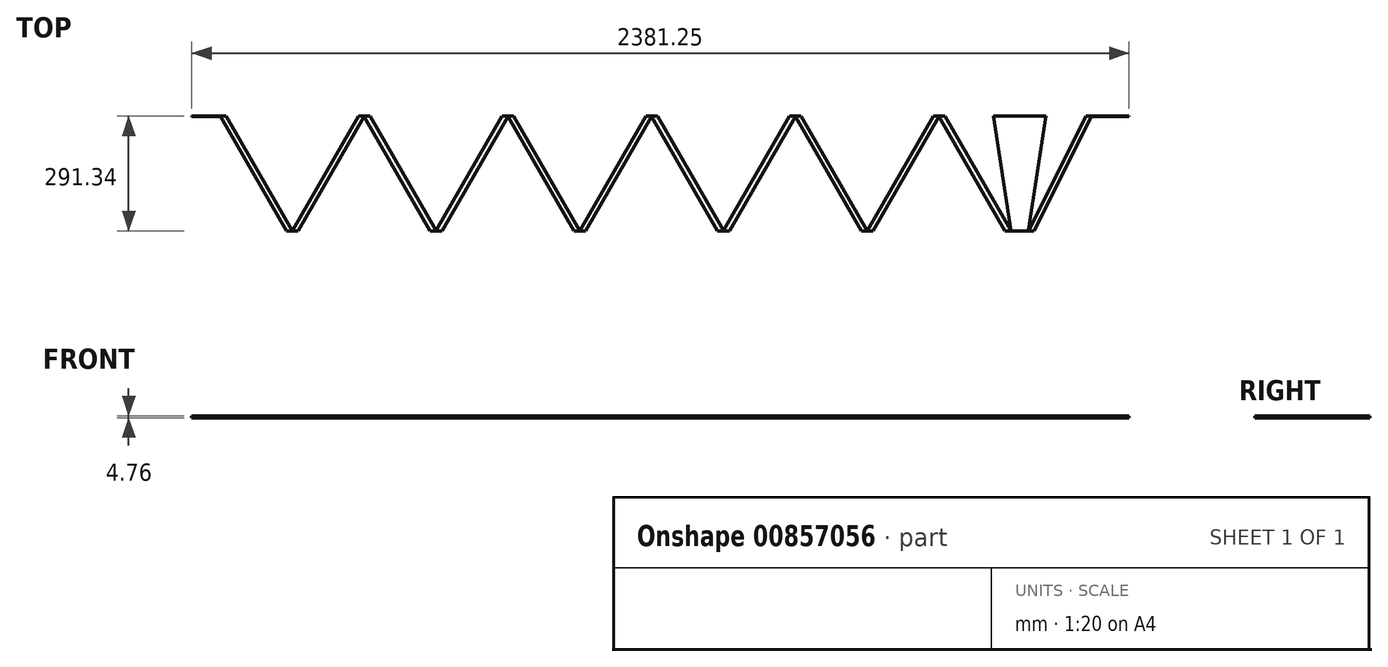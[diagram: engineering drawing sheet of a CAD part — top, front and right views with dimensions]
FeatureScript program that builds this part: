
annotation { "Feature Type Name" : "Feature", "Feature Type Description" : "" }
export const myFeature = defineFeature(function(context is Context, id is Id, definition is map)
    precondition{}
    {
        {
            var Q0;
            Q0=qCreatedBy(makeId("Top.planeOp"),FACE);
            var sketch = newSketch(context, id + "F0", { "sketchPlane" : qUnion([Q0])});
            skLineSegment(sketch, "E0.bottom", {"start": v(-1203.33, 145.67) * mm, "end": v(1203.33, 145.67) * mm});
            skLineSegment(sketch, "E0.top", {"start": v(-1203.33, -145.67) * mm, "end": v(1203.33, -145.67) * mm});
            skLineSegment(sketch, "E0.left", {"start": v(-1203.33, 145.67) * mm, "end": v(-1203.33, -145.67) * mm});
            skLineSegment(sketch, "E0.right", {"start": v(1203.33, 145.67) * mm, "end": v(1203.33, -145.67) * mm});
            skPoint(sketch, "E0.middle", {"position": v(0, 0) * mm});
            skPoint(sketch, "E1", {"position": v(0, 145.67) * mm});
            skPoint(sketch, "E2", {"position": v(0, -145.67) * mm});
            skPoint(sketch, "E3", {"position": v(182.56, -145.67) * mm});
            skPoint(sketch, "E4.MirrorP", {"position": v(-182.56, -145.67) * mm});
            skPoint(sketch, "E5", {"position": v(365.12, 145.67) * mm});
            skPoint(sketch, "E6", {"position": v(547.69, -145.67) * mm});
            skPoint(sketch, "E7", {"position": v(730.25, 145.67) * mm});
            skPoint(sketch, "E8", {"position": v(912.81, -145.67) * mm});
            skPoint(sketch, "E9", {"position": v(935.04, -145.67) * mm});
            skPoint(sketch, "E10", {"position": v(957.26, -145.67) * mm});
            skPoint(sketch, "E11", {"position": v(1117.6, 145.67) * mm});
            skLineSegment(sketch, "E12", {"start": v(0.22, 145.29) * mm, "end": v(167.9, -145.67) * mm});
            skLineSegment(sketch, "E13", {"start": v(182.34, -145.29) * mm, "end": v(14.66, 145.67) * mm});
            skLineSegment(sketch, "E14", {"start": v(182.78, -145.29) * mm, "end": v(350.47, 145.67) * mm});
            skLineSegment(sketch, "E15", {"start": v(364.9, 145.29) * mm, "end": v(197.22, -145.67) * mm});
            skLineSegment(sketch, "E16", {"start": v(365.35, 145.29) * mm, "end": v(533.03, -145.67) * mm});
            skLineSegment(sketch, "E17", {"start": v(547.47, -145.29) * mm, "end": v(379.78, 145.67) * mm});
            skLineSegment(sketch, "E18", {"start": v(547.9, -145.29) * mm, "end": v(715.6, 145.67) * mm});
            skLineSegment(sketch, "E19", {"start": v(730.03, 145.29) * mm, "end": v(562.35, -145.67) * mm});
            skLineSegment(sketch, "E20", {"start": v(730.47, 145.29) * mm, "end": v(898.15, -145.67) * mm});
            skLineSegment(sketch, "E21", {"start": v(912.14, -144.5) * mm, "end": v(744.9, 145.67) * mm});
            skLineSegment(sketch, "E22", {"start": v(957.98, -144.23) * mm, "end": v(1103.4, 145.67) * mm});
            skLineSegment(sketch, "E23", {"start": v(1117.6, 145.67) * mm, "end": v(971.47, -145.67) * mm});
            skLineSegment(sketch, "E24", {"start": v(-0.22, 145.29) * mm, "end": v(-167.9, -145.67) * mm});
            skLineSegment(sketch, "E25", {"start": v(-182.34, -145.29) * mm, "end": v(-14.66, 145.67) * mm});
            skPoint(sketch, "E26", {"position": v(-365.13, 145.67) * mm});
            skPoint(sketch, "E27", {"position": v(-730.25, 145.67) * mm});
            skPoint(sketch, "E28", {"position": v(-1095.38, 145.67) * mm});
            skLineSegment(sketch, "E29", {"start": v(-182.78, -145.29) * mm, "end": v(-350.47, 145.67) * mm});
            skLineSegment(sketch, "E30", {"start": v(-364.9, 145.29) * mm, "end": v(-197.22, -145.67) * mm});
            skLineSegment(sketch, "E31", {"start": v(-365.35, 145.29) * mm, "end": v(-533.03, -145.67) * mm});
            skPoint(sketch, "E32", {"position": v(-547.69, -145.67) * mm});
            skPoint(sketch, "E33", {"position": v(-912.81, -145.67) * mm});
            skLineSegment(sketch, "E34", {"start": v(-547.47, -145.29) * mm, "end": v(-379.78, 145.67) * mm});
            skLineSegment(sketch, "E35", {"start": v(-547.9, -145.29) * mm, "end": v(-715.6, 145.67) * mm});
            skLineSegment(sketch, "E36", {"start": v(-730.03, 145.29) * mm, "end": v(-562.35, -145.67) * mm});
            skLineSegment(sketch, "E37", {"start": v(-730.47, 145.29) * mm, "end": v(-898.15, -145.67) * mm});
            skLineSegment(sketch, "E38", {"start": v(-912.6, -145.29) * mm, "end": v(-744.9, 145.67) * mm});
            skLineSegment(sketch, "E39", {"start": v(-913.03, -145.29) * mm, "end": v(-1080.72, 145.67) * mm});
            skLineSegment(sketch, "E40", {"start": v(-1095.38, 145.67) * mm, "end": v(-927.47, -145.67) * mm});
            skArc(sketch, "E41.filletArc", {"start": v(-913.03, -145.29) * mm, "mid": v(-912.81, -145.41) * mm, "end": v(-912.6, -145.29) * mm});
            skArc(sketch, "E42.filletArc", {"start": v(-547.9, -145.29) * mm, "mid": v(-547.69, -145.41) * mm, "end": v(-547.47, -145.29) * mm});
            skArc(sketch, "E43.filletArc", {"start": v(-182.78, -145.29) * mm, "mid": v(-182.56, -145.41) * mm, "end": v(-182.34, -145.29) * mm});
            skArc(sketch, "E44.filletArc", {"start": v(182.34, -145.29) * mm, "mid": v(182.56, -145.41) * mm, "end": v(182.78, -145.29) * mm});
            skArc(sketch, "E45.filletArc", {"start": v(547.47, -145.29) * mm, "mid": v(547.69, -145.41) * mm, "end": v(547.9, -145.29) * mm});
            skArc(sketch, "E46.filletArc", {"start": v(730.47, 145.29) * mm, "mid": v(730.25, 145.41) * mm, "end": v(730.03, 145.29) * mm});
            skArc(sketch, "E47.filletArc", {"start": v(365.35, 145.29) * mm, "mid": v(365.12, 145.41) * mm, "end": v(364.9, 145.29) * mm});
            skArc(sketch, "E48.filletArc", {"start": v(0.22, 145.29) * mm, "mid": v(0, 145.41) * mm, "end": v(-0.22, 145.29) * mm});
            skArc(sketch, "E49.filletArc", {"start": v(-364.9, 145.29) * mm, "mid": v(-365.13, 145.41) * mm, "end": v(-365.35, 145.29) * mm});
            skArc(sketch, "E50.filletArc", {"start": v(-730.03, 145.29) * mm, "mid": v(-730.25, 145.41) * mm, "end": v(-730.47, 145.29) * mm});
            skLineSegment(sketch, "E51.bottom", {"start": v(1203.33, 145.67) * mm, "end": v(1225.55, 145.67) * mm});
            skLineSegment(sketch, "E51.top", {"start": v(1203.33, -145.67) * mm, "end": v(1225.55, -145.67) * mm});
            skLineSegment(sketch, "E51.right", {"start": v(1225.55, 145.67) * mm, "end": v(1225.55, -145.67) * mm});
            skLineSegment(sketch, "E52.bottom", {"start": v(-1203.33, 145.67) * mm, "end": v(-1181.1, 145.67) * mm});
            skLineSegment(sketch, "E52.top", {"start": v(-1203.33, -145.67) * mm, "end": v(-1181.1, -145.67) * mm});
            skLineSegment(sketch, "E52.right", {"start": v(-1181.1, 145.67) * mm, "end": v(-1181.1, -145.67) * mm});
            skLineSegment(sketch, "E53.bottom", {"start": v(-1181.1, 145.67) * mm, "end": v(-1168.4, 145.67) * mm});
            skLineSegment(sketch, "E53.top", {"start": v(-1181.1, -145.67) * mm, "end": v(-1168.4, -145.67) * mm});
            skLineSegment(sketch, "E53.right", {"start": v(-1168.4, 145.67) * mm, "end": v(-1168.4, -145.67) * mm});
            skLineSegment(sketch, "E54", {"start": v(-1203.33, 145.42) * mm, "end": v(-1095.23, 145.42) * mm});
            skLineSegment(sketch, "E55.bottom", {"start": v(1225.55, 145.67) * mm, "end": v(1212.85, 145.67) * mm});
            skLineSegment(sketch, "E55.top", {"start": v(1225.55, -145.67) * mm, "end": v(1212.85, -145.67) * mm});
            skLineSegment(sketch, "E55.right", {"start": v(1212.85, 145.67) * mm, "end": v(1212.85, -145.67) * mm});
            skLineSegment(sketch, "E56", {"start": v(1117.47, 145.42) * mm, "end": v(1212.85, 145.42) * mm});
            skLineSegment(sketch, "E57", {"start": v(912.6, -144.33) * mm, "end": v(868.36, 145.67) * mm});
            skLineSegment(sketch, "E58", {"start": v(957.5, -144.08) * mm, "end": v(1001.71, 145.67) * mm});
            skArc(sketch, "E59.filletArc", {"start": v(957.5, -144.08) * mm, "mid": v(957.68, -144.36) * mm, "end": v(957.98, -144.23) * mm});
            skArc(sketch, "E60.filletArc", {"start": v(912.14, -144.5) * mm, "mid": v(912.44, -144.61) * mm, "end": v(912.6, -144.33) * mm});
            skLineSegment(sketch, "E61", {"start": v(935.04, -145.67) * mm, "end": v(935.04, 145.67) * mm});
            skSolve(sketch);
        }
        {
            var Q0;
            {var subQ0=sQuery(id+"F0.wireOp",EDGE,"mt4UBC6S-nCec-m8ob-HfSP-5Ds3G4jtUm6S.bottom");Q0=makeQuery(id+"F0.imprint","IMPRINT",FACE,{"disambiguationData":[TD([[makeQuery(id+"F0.imprint","IMPRINT",EDGE,{"derivedFrom":subQ0}),-1.0]])]});}
            var Q1;
            {var subQ0=sQuery(id+"F0.wireOp",EDGE,"mt4UBC6S-nCec-m8ob-HfSP-5Ds3G4jtUm6S.top");Q1=makeQuery(id+"F0.imprint","IMPRINT",FACE,{"disambiguationData":[TD([[makeQuery(id+"F0.imprint","IMPRINT",EDGE,{"derivedFrom":subQ0}),1.0]])]});}
            var Q2;
            {var subQ1=sQuery(id+"F0.wireOp",EDGE,"E0.bottom");var subQ3=sQuery(id+"F0.wireOp",EDGE,"E40");var subQ4=makeQuery(id+"F0.imprint","INTERSECT",VERTEX,{"derivedFrom":[subQ1,subQ3]});Q2=makeQuery(id+"F0.imprint","IMPRINT",FACE,{"disambiguationData":[TD([[makeQuery(id+"F0.imprint","IMPRINT",EDGE,{"disambiguationData":[TD([[subQ4,-1.0]])],"derivedFrom":subQ3}),-1.0]])]});}
            var Q3;
            {var subQ5=sQuery(id+"F0.wireOp",EDGE,"YQS032Gt-JrIO-GTdh-uqIp-JOMJb26W4UZT");Q3=makeQuery(id+"F0.imprint","IMPRINT",FACE,{"disambiguationData":[TD([[makeQuery(id+"F0.imprint","IMPRINT",EDGE,{"derivedFrom":subQ5}),-1.0]])]});}
            var Q4;
            {var subQ0=sQuery(id+"F0.wireOp",EDGE,"E53.bottom");Q4=makeQuery(id+"F0.imprint","IMPRINT",FACE,{"disambiguationData":[TD([[makeQuery(id+"F0.imprint","IMPRINT",EDGE,{"derivedFrom":subQ0}),-1.0]])]});}
            var Q5;
            {var subQ0=sQuery(id+"F0.wireOp",EDGE,"E53.top");Q5=makeQuery(id+"F0.imprint","IMPRINT",FACE,{"disambiguationData":[TD([[makeQuery(id+"F0.imprint","IMPRINT",EDGE,{"derivedFrom":subQ0}),1.0]])]});}
            var Q6;
            {var subQ0=sQuery(id+"F0.wireOp",EDGE,"E22");var subQ1=sQuery(id+"F0.wireOp",EDGE,"E0.bottom");var subQ2=makeQuery(id+"F0.imprint","INTERSECT",VERTEX,{"derivedFrom":[subQ1,subQ0]});Q6=makeQuery(id+"F0.imprint","IMPRINT",FACE,{"disambiguationData":[TD([[makeQuery(id+"F0.imprint","IMPRINT",EDGE,{"disambiguationData":[TD([[subQ2,-1.0]])],"derivedFrom":subQ1}),-1.0]])]});}
            var Q7;
            {var subQ6=sQuery(id+"F0.wireOp",EDGE,"E12");Q7=makeQuery(id+"F0.imprint","IMPRINT",FACE,{"disambiguationData":[TD([[makeQuery(id+"F0.imprint","IMPRINT",EDGE,{"derivedFrom":subQ6}),1.0]])]});}
            var Q8;
            Q8=makeQuery(id+"F0.imprint","IMPRINT",FACE,{"disambiguationData":[TD([[makeQuery(id+"F0.imprint","IMPRINT",EDGE,{"derivedFrom":sQuery(id+"F0.wireOp",EDGE,"E55.bottom")}),1.0]])]});
            var Q9;
            {var subQ1=sQuery(id+"F0.wireOp",EDGE,"E0.bottom");var subQ3=sQuery(id+"F0.wireOp",EDGE,"E23");var subQ4=makeQuery(id+"F0.imprint","INTERSECT",VERTEX,{"derivedFrom":[subQ1,subQ3]});Q9=makeQuery(id+"F0.imprint","IMPRINT",FACE,{"disambiguationData":[TD([[makeQuery(id+"F0.imprint","IMPRINT",EDGE,{"disambiguationData":[TD([[subQ4,-1.0]])],"derivedFrom":subQ3}),1.0]])]});}
            var Q10;
            {var subQ0=sQuery(id+"F0.wireOp",EDGE,"E51.bottom");Q10=makeQuery(id+"F0.imprint","IMPRINT",FACE,{"disambiguationData":[TD([[makeQuery(id+"F0.imprint","IMPRINT",EDGE,{"derivedFrom":subQ0}),-1.0]])]});}
            var Q11;
            {var subQ0=sQuery(id+"F0.wireOp",EDGE,"E57");Q11=makeQuery(id+"F0.imprint","IMPRINT",FACE,{"disambiguationData":[TD([[makeQuery(id+"F0.imprint","IMPRINT",EDGE,{"derivedFrom":subQ0}),-1.0]])]});}
            extrude(context, id + "F1", {"entities" : qUnion([Q0, Q1, Q2, Q3, Q4, Q5, Q6, Q7, Q8, Q9, Q10, Q11]), "depth" : 4.76 * mm, "offsetDistance" : 25.4 * mm});
        }
    });
